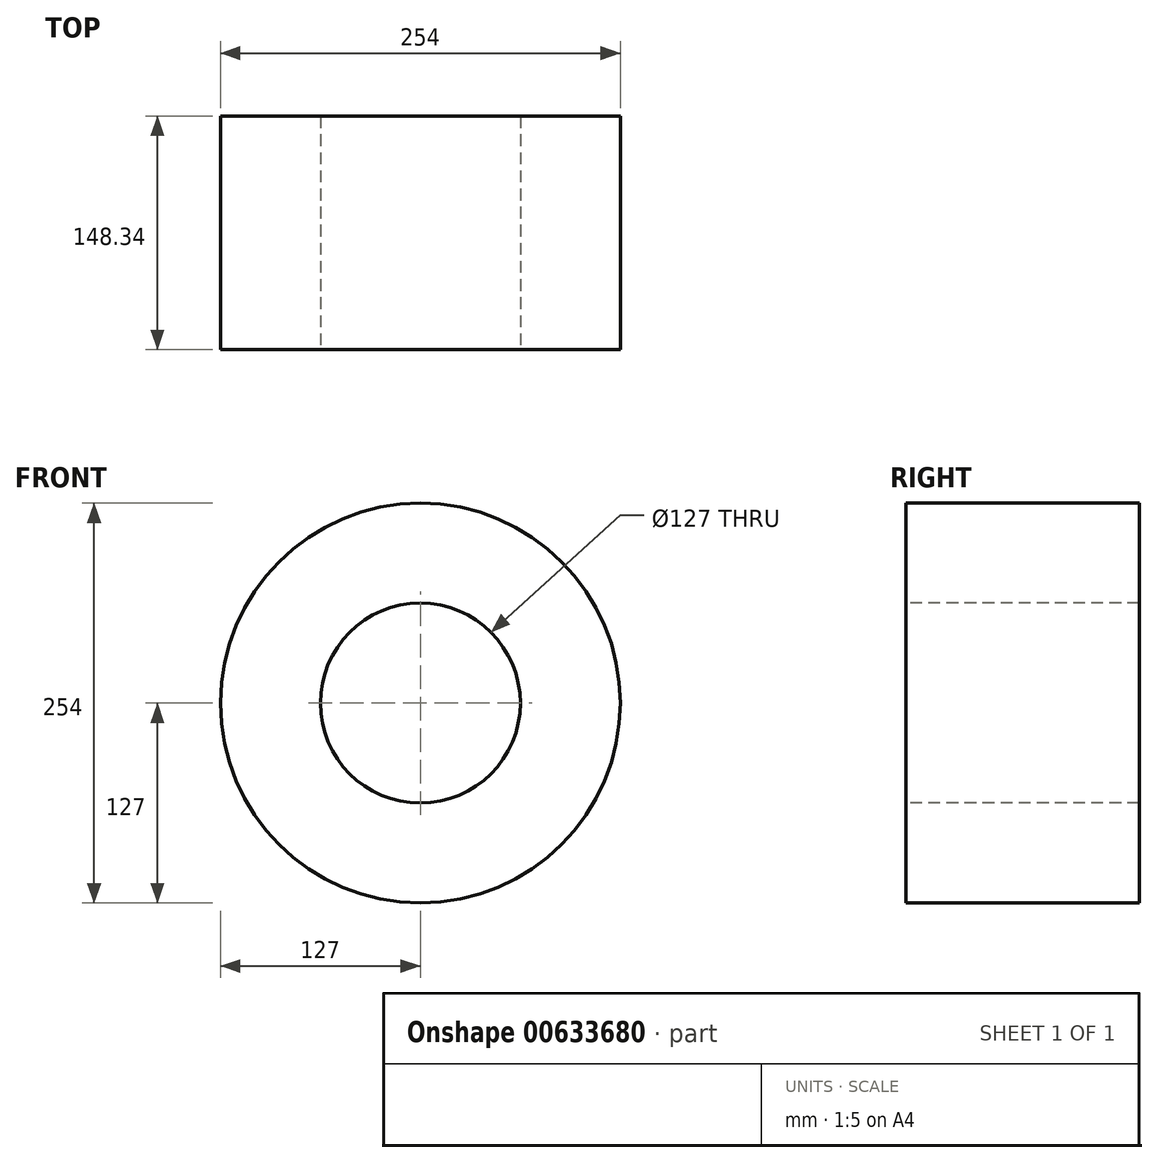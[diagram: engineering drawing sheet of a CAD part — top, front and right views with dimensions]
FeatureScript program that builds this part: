
annotation { "Feature Type Name" : "Feature", "Feature Type Description" : "" }
export const myFeature = defineFeature(function(context is Context, id is Id, definition is map)
    precondition{}
    {
        {
            var Q0;
            Q0=qCreatedBy(makeId("Front.planeOp"),FACE);
            var sketch = newSketch(context, id + "F0", { "sketchPlane" : qUnion([Q0])});
            skCircle(sketch, "E0", {"center": v(0, 0) * mm, "radius": 63.5 * mm});
            skSolve(sketch);
        }
        {
            var Q0;
            Q0=qCreatedBy(makeId("Right.planeOp"),FACE);
            var sketch = newSketch(context, id + "F1", { "sketchPlane" : qUnion([Q0])});
            skLineSegment(sketch, "E1", {"start": v(0, 0) * mm, "end": v(179.43, 0) * mm});
            skSolve(sketch);
        }
        {
            var Q0;
            Q0=qCreatedBy(makeId("Front.planeOp"),FACE);
            var sketch = newSketch(context, id + "F2", { "sketchPlane" : qUnion([Q0])});
            skCircle(sketch, "E2", {"center": v(0, 0) * mm, "radius": 127 * mm});
            skSolve(sketch);
        }
        {
            var Q0;
            Q0 = qSketchRegion(id + "F2", true);
            extrude(context, id + "F3", {"entities" : qUnion([Q0]), "oppositeDirection" : true, "depth" : 148.34 * mm, "offsetDistance" : 25.4 * mm});
        }
        {
            var Q0;
            Q0=makeQuery(id+"F0.imprint","IMPRINT",FACE,{"disambiguationData":[TD([[makeQuery(id+"F0.imprint","IMPRINT",EDGE,{"derivedFrom":sQuery(id+"F0.wireOp",EDGE,"E0")}),1.0]])]});
            extrude(context, id + "F4", {"entities" : qUnion([Q0]), "operationType" : NewBodyOperationType.REMOVE, "oppositeDirection" : true, "depth" : 280.92 * mm, "offsetDistance" : 25.4 * mm, "hasSecondDirection" : true, "secondDirectionOppositeDirection" : false, "secondDirectionDepth" : 25.4 * mm});
        }
    });
